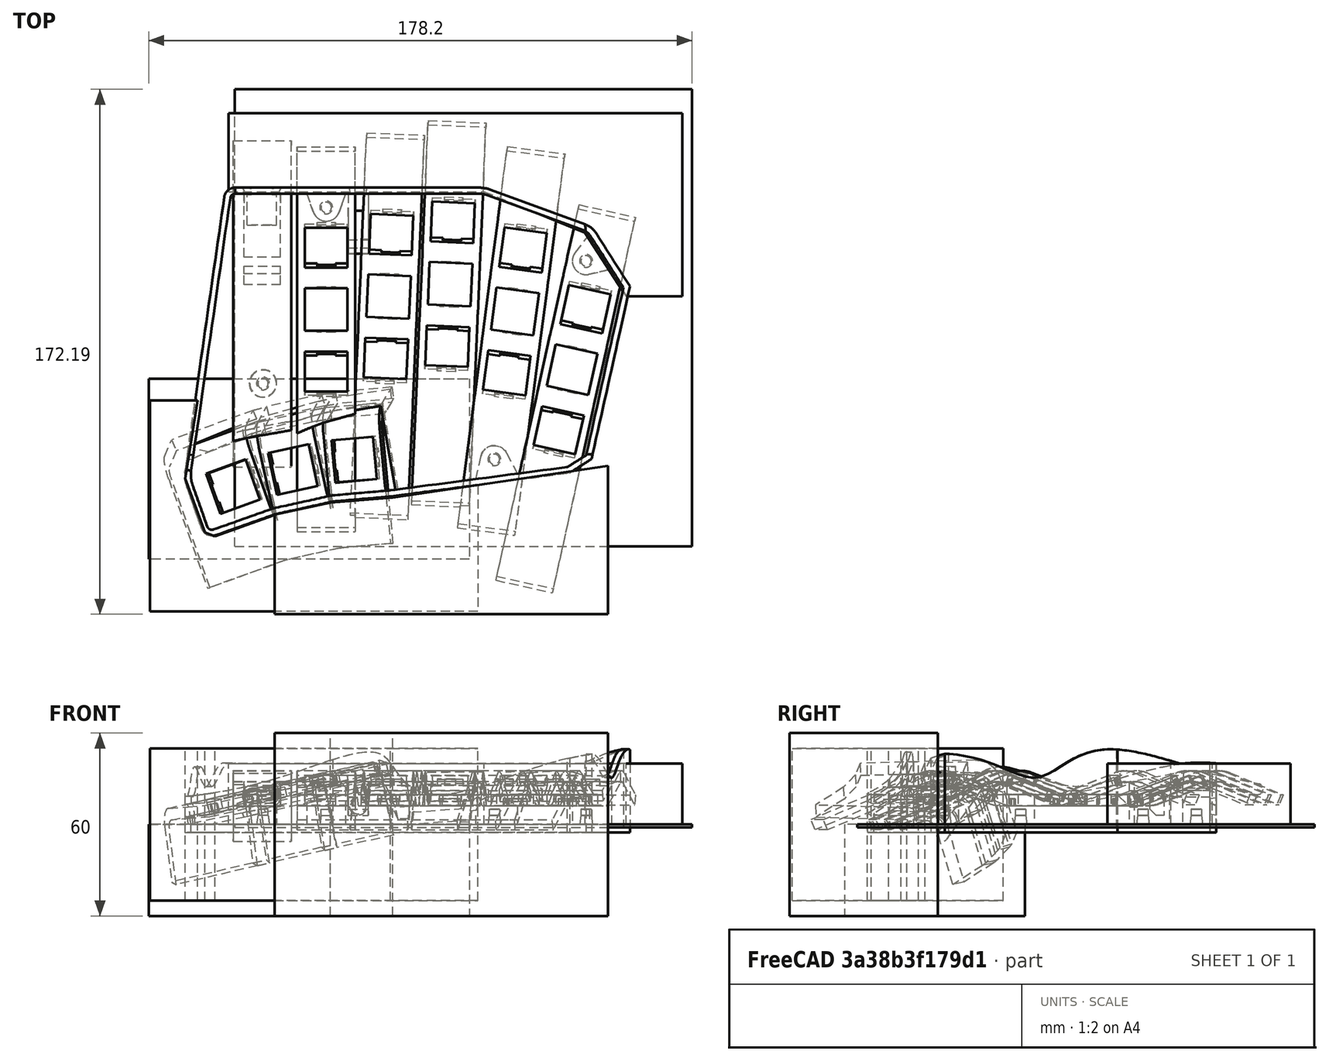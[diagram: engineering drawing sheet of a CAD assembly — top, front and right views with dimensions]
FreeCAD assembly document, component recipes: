
FREECAD ASSEMBLY — COMPONENT RECIPES ("KeyColumnArray2")

This assembly document has 28 components, labeled P0..P27 below (a component is one placed body or linked part). 20 of them carry a construction recipe — the FreeCAD feature program that regenerates the part from scratch, quoted from this document or its linked companion documents; the rest are supplied as boundary geometry only. No exploded tour is included for this assembly.
COMPONENT P0 — recipe-attached ("ShellRough", modeled in this document).
Construction recipe (the document's own serialized feature program — sketch geometry with constraints, then the solid features built on it; lengths are millimeters unless a unit is written):

FEATURE [Sketcher::SketchObject] Sketch
  FullyConstrained = false
  MapMode = 5
  Support = -> [XY_Plane001]
  sketch-geometry (20):
    g0: LineSegment StartX=-33.4431 StartY=36.9112 StartZ=0 EndX=-46.2795 EndY=-52.5754 EndZ=0
    g1: LineSegment StartX=-45.7128 StartY=-58.285 StartZ=0 EndX=-40.9023 EndY=-71.8694 EndZ=0
    g2: LineSegment StartX=-36.307 StartY=-74.0612 StartZ=0 EndX=-16.9221 EndY=-67.1967 EndZ=0
    g3: LineSegment StartX=-16.9221 StartY=-67.1967 StartZ=0 EndX=2.15083 EndY=-62.9753 EndZ=0
    g4: LineSegment StartX=2.15083 StartY=-62.9753 StartZ=0 EndX=21.2304 EndY=-61.306 EndZ=0
    g5: LineSegment StartX=21.2304 StartY=-61.306 StartZ=0 EndX=79.8355 EndY=-53.6064 EndZ=0
    g6: LineSegment StartX=79.8355 StartY=-53.6064 StartZ=0 EndX=87.0661 EndY=-49 EndZ=0
    g7: LineSegment StartX=87.0661 StartY=-49 StartZ=0 EndX=99.6141 EndY=7.6 EndZ=0
    g8: LineSegment StartX=99.6141 StartY=7.6 StartZ=0 EndX=88.4546 EndY=25.1169 EndZ=0
    g9: LineSegment StartX=84.9582 StartY=27.9288 StartZ=0 EndX=53.9986 EndY=39.268 EndZ=0
    g10: LineSegment StartX=49.8716 StartY=40 StartZ=0 EndX=-29.8796 EndY=40 EndZ=0
    g11: ArcOfCircle CenterX=-37.5088 CenterY=-70.6677 CenterZ=0 NormalX=0 NormalY=0 NormalZ=1 AngleXU=0 Radius=3.6 StartAngle=3.48193 EndAngle=5.05273
    g12: ArcOfCircle CenterX=-29.8796 CenterY=36.4 CenterZ=0 NormalX=0 NormalY=0 NormalZ=1 AngleXU=0 Radius=3.6 StartAngle=1.5708 EndAngle=2.99912
    g13: GeomPoint X=-33 Y=40 Z=0
    g14: ArcOfCircle CenterX=-34.4011 CenterY=-54.2793 CenterZ=0 NormalX=0 NormalY=0 NormalZ=1 AngleXU=0 Radius=12 StartAngle=2.99912 EndAngle=3.48193
    g15: GeomPoint X=-46.699 Y=-55.5 Z=0
    g16: ArcOfCircle CenterX=49.8716 CenterY=28 CenterZ=0 NormalX=0 NormalY=0 NormalZ=1 AngleXU=0 Radius=12 StartAngle=1.21971 EndAngle=1.5708
    g17: GeomPoint X=52 Y=40 Z=0
    g18: ArcOfCircle CenterX=82.5508 CenterY=21.3558 CenterZ=0 NormalX=0 NormalY=0 NormalZ=1 AngleXU=0 Radius=7 StartAngle=0.567232 EndAngle=1.21971
    g19: GeomPoint X=87.1821 Y=27.1143 Z=0
  constraints (43):
    c: Coincident(g2,g3)
    c: Coincident(g3,g4)
    c: Coincident(g4,g5)
    c: Coincident(g5,g6)
    c: Coincident(g6,g7)
    c: Coincident(g7,g8)
    c: Horizontal(g10)
    c: DistanceY(g-1,g17) = 40
    c: DistanceX(g-1,g17) = 52
    c: DistanceX(g13,g-1) = 33
    c: Angle(g-1,g7) = 1.35263
    c: Angle(g7,g6) = 2.35619
    c: Perpendicular(g2,g1)
    c: Angle(g-2,g1) = 0.340339
    c: DistanceY(g15,g-1) = 55.5
    c: Tangent(g1,g11) = -1.5708
    c: Tangent(g2,g11) = -1.5708
    c: Radius(g11) = 3.6
    c: Angle(g-2,g3) = 1.78861
    c: Angle(g4,g-2) = 1.48353
    c: PointOnObject(g13,g0)
    c: PointOnObject(g13,g10)
    c: Tangent(g0,g12) = -1.5708
    c: Tangent(g10,g12) = -1.5708
    c: Radius(g12) = 3.6
    c: PointOnObject(g15,g1)
    c: PointOnObject(g15,g0)
    c: Tangent(g1,g14) = -1.5708
    c: Tangent(g0,g14) = -1.5708
    c: Radius(g14) = 12
    c: PointOnObject(g17,g10)
    c: PointOnObject(g17,g9)
    c: Tangent(g10,g16) = -1.5708
    c: Tangent(g9,g16) = -1.5708
    c: Radius(g16) = 12
    c: PointOnObject(g19,g9)
    c: PointOnObject(g19,g8)
    c: Tangent(g9,g18) = -1.5708
    c: Tangent(g8,g18) = -1.5708
    c: Radius(g18) = 7
    c: Angle(g8,g7) = 2.35619
    c: DistanceY(g-1,g7) = 7.6
    c: DistanceY(g6,g-1) = 49
FEATURE [PartDesign::Pad] Pad
  Direction = (0,0,1)
  Length = 30
  Length2 = 10
  Profile = -> Sketch
  ReferenceAxis = -> Sketch [N_Axis]
  Type = 0
FEATURE [PartDesign::Thickness] Thickness
  Base = -> Pad [Face18,Face17]
  BaseFeature = -> Pad
  Intersection = false
  Join = 0
  Mode = 0
  Reversed = true
  SupportTransform = false
  Value = 2
FEATURE [PartDesign::Body] Body001  label="ShellRough"
  Group = -> [Sketch,Pad,Thickness]
  Origin = -> Origin001
  Tip = -> Thickness
COMPONENT P1 — recipe-attached ("ThumbCutterBotLeft", modeled in this document).
Construction recipe (the document's own serialized feature program — sketch geometry with constraints, then the solid features built on it; lengths are millimeters unless a unit is written):

FEATURE [Sketcher::SketchObject] Sketch002
  FullyConstrained = false
  MapMode = 5
  Support = -> [XY_Plane003]
  sketch-geometry (11):
    g0: LineSegment StartX=-57.8461 StartY=-29.8467 StartZ=0 EndX=-42.1659 EndY=-29.8467 EndZ=0
    g1: LineSegment StartX=-42.1659 StartY=-29.8467 StartZ=0 EndX=-46.2211 EndY=-55.5298 EndZ=0
    g2: LineSegment StartX=-46.2211 StartY=-55.5298 StartZ=0 EndX=-39.7328 EndY=-73.1024 EndZ=0
    g3: LineSegment StartX=-39.7328 StartY=-73.1024 StartZ=0 EndX=-36.4886 EndY=-74.4541 EndZ=0
    g4: LineSegment StartX=-36.4886 StartY=-74.4541 StartZ=0 EndX=-17.0235 EndY=-67.4251 EndZ=0
    g5: LineSegment StartX=-17.0235 StartY=-67.4251 StartZ=0 EndX=1.36017 EndY=-63.3699 EndZ=0
    g6: LineSegment StartX=1.36017 StartY=-63.3699 StartZ=0 EndX=21.0956 EndY=-61.4774 EndZ=0
    g7: LineSegment StartX=21.0956 StartY=-61.4774 StartZ=0 EndX=49.7525 EndY=-57.6925 EndZ=0
    g8: LineSegment StartX=49.7525 StartY=-57.6925 StartZ=0 EndX=49.7525 EndY=-99.0559 EndZ=0
    g9: LineSegment StartX=49.7525 StartY=-99.0559 StartZ=0 EndX=-57.8461 EndY=-99.0559 EndZ=0
    g10: LineSegment StartX=-57.8461 StartY=-99.0559 StartZ=0 EndX=-57.8461 EndY=-29.8467 EndZ=0
  constraints (15):
    c: Horizontal(g0)
    c: Coincident(g0,g1)
    c: Coincident(g1,g2)
    c: Coincident(g2,g3)
    c: Coincident(g3,g4)
    c: Coincident(g4,g5)
    c: Coincident(g5,g6)
    c: Coincident(g6,g7)
    c: Coincident(g7,g8)
    c: Vertical(g8)
    c: Coincident(g8,g9)
    c: Horizontal(g9)
    c: Coincident(g9,g10)
    c: Coincident(g10,g0)
    c: Vertical(g10)
FEATURE [PartDesign::Pad] Pad002
  Direction = (0,0,1)
  Length = 50
  Length2 = 10
  Midplane = true
  Profile = -> Sketch002
  ReferenceAxis = -> Sketch002 [N_Axis]
  Type = 0
FEATURE [PartDesign::Body] Body003  label="ThumbCutterBotLeft"
  Group = -> [Sketch002,Pad002]
  Origin = -> Origin003
  Tip = -> Pad002
COMPONENT P2 — recipe-attached ("ThumbCutterBottom", modeled in this document).
Construction recipe (the document's own serialized feature program — sketch geometry with constraints, then the solid features built on it; lengths are millimeters unless a unit is written):

FEATURE [Sketcher::SketchObject] Sketch003
  FullyConstrained = false
  MapMode = 5
  Support = -> [XY_Plane004]
  sketch-geometry (4):
    g0: LineSegment StartX=-58.202 StartY=-22.7672 StartZ=0 EndX=46.9496 EndY=-22.7672 EndZ=0
    g1: LineSegment StartX=46.9496 StartY=-22.7672 StartZ=0 EndX=46.9496 EndY=-81.8868 EndZ=0
    g2: LineSegment StartX=46.9496 StartY=-81.8868 StartZ=0 EndX=-58.202 EndY=-81.8868 EndZ=0
    g3: LineSegment StartX=-58.202 StartY=-81.8868 StartZ=0 EndX=-58.202 EndY=-22.7672 EndZ=0
  constraints (8):
    c: Coincident(g0,g1)
    c: Coincident(g1,g2)
    c: Coincident(g2,g3)
    c: Coincident(g3,g0)
    c: Horizontal(g0)
    c: Horizontal(g2)
    c: Vertical(g1)
    c: Vertical(g3)
FEATURE [PartDesign::Pad] Pad003
  Direction = (0,0,1)
  Length = 30
  Length2 = 10
  Profile = -> Sketch003
  ReferenceAxis = -> Sketch003 [N_Axis]
  Reversed = true
  Type = 0
FEATURE [PartDesign::Body] Body004  label="ThumbCutterBottom"
  Group = -> [Sketch003,Pad003]
  Origin = -> Origin004
  Tip = -> Pad003
COMPONENT P3 — recipe-attached ("UnderThumbCutter", modeled in this document).
Construction recipe (the document's own serialized feature program — sketch geometry with constraints, then the solid features built on it; lengths are millimeters unless a unit is written):

FEATURE [PartDesign::SubShapeBinder] Binder003  label="Big"
  BindCopyOnChange = 0
  BindMode = 0
  ClaimChildren = false
  Context = -> Body006 [Binder003.]
  Fuse = false
  MakeFace = true
  OffsetFill = false
  OffsetIntersection = false
  OffsetJoinType = 0
  OffsetOpenResult = false
  PartialLoad = false
  Relative = true
  Support = -> [Cut002[Edge44,Edge45,Edge46,Edge47]]
  _Version = 2
FEATURE [PartDesign::SubShapeBinder] Binder004  label="Small"
  BindCopyOnChange = 0
  BindMode = 0
  ClaimChildren = false
  Context = -> Body006 [Binder004.]
  Fuse = false
  MakeFace = true
  OffsetFill = false
  OffsetIntersection = false
  OffsetJoinType = 0
  OffsetOpenResult = false
  PartialLoad = false
  Relative = true
  Support = -> [Cut002[Edge127,Edge129,Edge130,Edge131]]
  _Version = 2
FEATURE [PartDesign::SubShapeBinder] Binder005  label="Path"
  BindCopyOnChange = 0
  BindMode = 0
  ClaimChildren = false
  Context = -> Body006 [Binder005.]
  Fuse = false
  MakeFace = true
  OffsetFill = false
  OffsetIntersection = false
  OffsetJoinType = 0
  OffsetOpenResult = false
  PartialLoad = false
  Relative = true
  Support = -> [Cut002[Edge127,Edge126,Edge123,Edge122,Edge109]]
  _Version = 2
FEATURE [Sketcher::SketchObject] Sketch005
  FullyConstrained = false
  Placement = pos=(-2.47193,-0.548013,11.4209) rot=(0.216439,-0.976296,0;0.218166rad)
  sketch-geometry (5):
    g0: LineSegment StartX=21.4334 StartY=-34.223 StartZ=0 EndX=2.51313 EndY=-35.9615 EndZ=0
    g1: BSplineCurve PolesCount=2 KnotsCount=2 Degree=1 IsPeriodic=0
    g2: LineSegment StartX=-1.05539 StartY=-36.5965 StartZ=0 EndX=-19.605 EndY=-40.7088 EndZ=0
    g3: BSplineCurve PolesCount=2 KnotsCount=2 Degree=1 IsPeriodic=0
    g4: LineSegment StartX=-23.1076 StartY=-41.6414 StartZ=0 EndX=-40.9899 EndY=-48.0619 EndZ=0
  constraints (4):
    c: Coincident(g0,g1)
    c: Coincident(g1,g2)
    c: Coincident(g2,g3)
    c: Coincident(g3,g4)
FEATURE [Sketcher::SketchObject] Sketch006
  FullyConstrained = false
  Placement = pos=(-50.3364,-18.2454,-11.7703) rot=(0.340774,-0.940145,0;1.78719rad)
  sketch-geometry (4):
    g0: LineSegment StartX=34.9538 StartY=-48.5618 StartZ=0 EndX=33.5799 EndY=-45.0789 EndZ=0
    g1: LineSegment StartX=33.5799 StartY=-45.0789 StartZ=0 EndX=26.6082 EndY=-27.4042 EndZ=0
    g2: ArcOfCircle CenterX=22.8872 CenterY=-28.8719 CenterZ=0 NormalX=0 NormalY=1e-16 NormalZ=1 AngleXU=-2.76588 Radius=4 StartAngle=1.5708 EndAngle=2.88852
    g3: LineSegment StartX=21.8685 StartY=-24.9672 StartZ=0 EndX=22.3979 EndY=-24.902 EndZ=0
  constraints (3):
    c: Coincident(g0,g1)
    c: Coincident(g1,g2)
    c: Coincident(g2,g3)
FEATURE [Sketcher::SketchObject] Sketch007
  FullyConstrained = false
  Placement = pos=(17.7176,1.57374,3.9103) rot=(-0.088475,0.996078,0;1.3544rad)
  sketch-geometry (6):
    g0: LineSegment StartX=-9.09004 StartY=-79.2968 StartZ=0 EndX=-11.138 EndY=-61.1386 EndZ=0
    g1: LineSegment StartX=-11.138 StartY=-61.1386 StartZ=0 EndX=-13.3253 EndY=-42.1061 EndZ=0
    g2: ArcOfCircle CenterX=-5.98227 CenterY=-40.8863 CenterZ=0 NormalX=1e-16 NormalY=0 NormalZ=1 AngleXU=-1.45423 Radius=7.44361 StartAngle=3.36428 EndAngle=4.76043
    g3: LineSegment StartX=9.38655 StartY=-26.7286 StartZ=0 EndX=-8.45934 EndY=-33.867 EndZ=0
    g4: LineSegment StartX=-9.09004 StartY=-79.2968 StartZ=0 EndX=18.9825 EndY=-76.3619 EndZ=0
    g5: LineSegment StartX=18.9825 StartY=-76.3619 StartZ=0 EndX=9.38655 EndY=-26.7286 EndZ=0
  constraints (6):
    c: Coincident(g0,g1)
    c: Coincident(g1,g2)
    c: Coincident(g2,g3)
    c: Coincident(g0,g4)
    c: Coincident(g4,g5)
    c: Coincident(g5,g3)
FEATURE [PartDesign::AdditivePipe] AdditivePipe
  AuxilleryCurvelinear = true
  AuxillerySpineTangent = false
  Binormal = (0,0,0)
  Mode = 0
  Placement = pos=(17.7176,1.57374,3.9103) rot=(-0.088475,0.996078,0;1.3544rad)
  Profile = -> Sketch007
  Spine = -> Binder005
  SpineTangent = false
  Transformation = 0
  Transition = 0
FEATURE [PartDesign::Body] Body006  label="UnderThumbCutter"
  Group = -> [Binder003,Binder004,Binder005,Sketch005,Sketch006,Sketch007,AdditivePipe]
  Origin = -> Origin006
  Tip = -> AdditivePipe
COMPONENT P4 — recipe-attached ("MCU-Holder", modeled in this document).
Construction recipe (the document's own serialized feature program — sketch geometry with constraints, then the solid features built on it; lengths are millimeters unless a unit is written):

FEATURE [Sketcher::SketchObject] Sketch008
  FullyConstrained = true
  MapMode = 5
  Placement = pos=(0,0,0) rot=(0.57735,0.57735,0.57735;2.0944rad)
  Support = -> [YZ_Plane007]
  sketch-geometry (8):
    g0: LineSegment StartX=-24 StartY=5.5 StartZ=0 EndX=-24 EndY=0 EndZ=0
    g1: LineSegment StartX=-24 StartY=0 StartZ=0 EndX=1.25 EndY=0 EndZ=0
    g2: LineSegment StartX=1.25 StartY=0 StartZ=0 EndX=1.25 EndY=-3.6 EndZ=0
    g3: LineSegment StartX=1.25 StartY=-3.6 StartZ=0 EndX=-4.9788 EndY=-4.78813 EndZ=0
    g4: LineSegment StartX=-4.9788 StartY=-4.78813 StartZ=0 EndX=-30.1 EndY=0 EndZ=0
    g5: LineSegment StartX=-30.1 StartY=0 StartZ=0 EndX=-30.1 EndY=2 EndZ=0
    g6: LineSegment StartX=-30.1 StartY=2 StartZ=0 EndX=-26.6 EndY=5.5 EndZ=0
    g7: LineSegment StartX=-26.6 StartY=5.5 StartZ=0 EndX=-24 EndY=5.5 EndZ=0
  constraints (24):
    c: PointOnObject(g0,g-1)
    c: Vertical(g0)
    c: Coincident(g0,g1)
    c: Horizontal(g1)
    c: Coincident(g1,g2)
    c: Vertical(g2)
    c: Coincident(g2,g3)
    c: Coincident(g3,g4)
    c: PointOnObject(g4,g-1)
    c: Coincident(g4,g5)
    c: Vertical(g5)
    c: Coincident(g5,g6)
    c: Coincident(g6,g7)
    c: Coincident(g7,g0)
    c: Horizontal(g7)
    c: DistanceX(g7,g7) = 2.6
    c: DistanceY(g0,g0) = 5.5
    c: DistanceX(g5,g6) = 3.5
    c: Angle(g6,g7) = 2.35619
    c: DistanceX(g0,g-1) = 24
    c: DistanceX(g-1,g1) = 1.25
    c: DistanceY(g2,g2) = 3.6
    c: DistanceX(g3) = -4.9788
    c: DistanceY(g3) = -4.78813
FEATURE [PartDesign::Pad] Pad005
  Direction = (1,-2e-16,3e-16)
  Length = 12
  Length2 = 10
  Midplane = true
  Placement = pos=(0,0,0) rot=(0.57735,0.57735,0.57735;2.0944rad)
  Profile = -> Sketch008
  ReferenceAxis = -> Sketch008 [N_Axis]
  Type = 0
FEATURE [PartDesign::Body] Body007  label="MCU-Holder"
  Group = -> [Sketch008,Pad005]
  Origin = -> Origin007
  Placement = pos=(-21,38.25,11.25) rot=(0,1,0;3.14159rad)
  Tip = -> Pad005
COMPONENT P5 — geometry summary ("ShellCutterPart"; no construction recipe available for this part):
  bounding box: 146.0 x 114.3 x 30.0 mm
  tessellated surface: 412 triangles
  volume: 395667 mm^3 (79% of its bounding box)
  symmetry: mirror-symmetric across its z mid-plane
COMPONENT P6 — recipe-attached ("ThumbTriangleCutter", modeled in this document).
Construction recipe (the document's own serialized feature program — sketch geometry with constraints, then the solid features built on it; lengths are millimeters unless a unit is written):

FEATURE [PartDesign::SubShapeBinder] Binder008
  BindCopyOnChange = 0
  BindMode = 0
  ClaimChildren = false
  Context = -> Body010 [Binder008.]
  Fuse = false
  MakeFace = true
  OffsetFill = false
  OffsetIntersection = false
  OffsetJoinType = 0
  OffsetOpenResult = false
  PartialLoad = false
  Relative = true
  Support = -> [Common[Face16,Face15,Face14,Face13,Face12]]
  _Version = 2
FEATURE [PartDesign::SubShapeBinder] Binder009
  BindCopyOnChange = 0
  BindMode = 0
  ClaimChildren = false
  Context = -> Body010 [Binder009.]
  Fuse = false
  MakeFace = true
  OffsetFill = false
  OffsetIntersection = false
  OffsetJoinType = 0
  OffsetOpenResult = false
  PartialLoad = false
  Relative = true
  Support = -> [Common[Face6,Face7,Face8,Face9,Face10]]
  _Version = 2
FEATURE [PartDesign::Plane] DatumPlane
  Length = 90.3213
  MapMode = 45
  Placement = pos=(10.8462,-31.5971,6.48979) rot=(-0.487707,-0.562269,-0.667829;1.80626rad)
  ResizeMode = 0
  Support = -> [Binder008,Binder009]
  Width = 97.1376
FEATURE [Sketcher::SketchObject] Sketch010
  FullyConstrained = false
  MapMode = 5
  Placement = pos=(10.8462,-31.5971,6.48979) rot=(-0.487707,-0.562269,-0.667829;1.80626rad)
  Support = -> [DatumPlane]
  sketch-geometry (7):
    g0: LineSegment StartX=-5.99127 StartY=-62.4069 StartZ=0 EndX=-2.7146 EndY=-38.9241 EndZ=0
    g1: LineSegment StartX=-2.7146 StartY=-38.9241 StartZ=0 EndX=-1.48585 EndY=-31.6881 EndZ=0
    g2: LineSegment StartX=-1.48585 StartY=-31.6881 StartZ=0 EndX=1.51776 EndY=-16.1239 EndZ=0
    g3: LineSegment StartX=1.51776 StartY=-16.1239 StartZ=0 EndX=2.88304 EndY=-9.5706 EndZ=0
    g4: LineSegment StartX=2.88304 StartY=-9.5706 StartZ=0 EndX=7.38846 EndY=8.9972 EndZ=0
    g5: LineSegment StartX=7.38846 StartY=8.9972 StartZ=0 EndX=-10.3602 EndY=14.0487 EndZ=0
    g6: LineSegment StartX=-10.3602 StartY=14.0487 StartZ=0 EndX=-5.99127 EndY=-62.4069 EndZ=0
  constraints (7):
    c: Coincident(g0,g1)
    c: Coincident(g1,g2)
    c: Coincident(g2,g3)
    c: Coincident(g3,g4)
    c: Coincident(g4,g5)
    c: Coincident(g5,g6)
    c: Coincident(g6,g0)
FEATURE [PartDesign::Pad] Pad007
  Direction = (-0.145065,0.93735,0.31675)
  Length = 20
  Length2 = 10
  Midplane = true
  Placement = pos=(10.8462,-31.5971,6.48979) rot=(-0.487707,-0.562269,-0.667829;1.80626rad)
  Profile = -> Sketch010
  ReferenceAxis = -> Sketch010 [N_Axis]
  Type = 0
FEATURE [PartDesign::Body] Body010  label="ThumbTriangleCutter"
  Group = -> [Binder008,Binder009,DatumPlane,Sketch010,Pad007]
  Origin = -> Origin010
  Tip = -> Pad007
COMPONENT P7 — recipe-attached ("WaveFront", modeled in this document).
Construction recipe (the document's own serialized feature program — sketch geometry with constraints, then the solid features built on it; lengths are millimeters unless a unit is written):

FEATURE [Sketcher::SketchObject] Sketch011
  FullyConstrained = false
  MapMode = 5
  Placement = pos=(0,0,0) rot=(1,0,0;1.5708rad)
  Support = -> [XZ_Plane011]
  sketch-geometry (23):
    g0: LineSegment StartX=-51.25 StartY=39.47 StartZ=0 EndX=-51.25 EndY=8.74275 EndZ=0
    g1: LineSegment StartX=-51.25 StartY=8.74275 StartZ=0 EndX=18.1024 EndY=24.754 EndZ=0
    g2: LineSegment StartX=22.4199 StartY=22.0561 StartZ=0 EndX=24.2026 EndY=14.3346 EndZ=0
    g3: LineSegment StartX=28.2541 StartY=11.5857 StartZ=0 EndX=107.47 EndY=23.6899 EndZ=0
    g4: LineSegment StartX=107.47 StartY=23.6899 StartZ=0 EndX=107.47 EndY=39.47 EndZ=0
    g5: LineSegment StartX=107.47 StartY=39.47 StartZ=0 EndX=-51.25 EndY=39.47 EndZ=0
    g6: ArcOfCircle CenterX=18.9122 CenterY=21.2463 CenterZ=0 NormalX=0 NormalY=0 NormalZ=1 AngleXU=0 Radius=3.6 StartAngle=0.226893 EndAngle=1.79769
    g7: ArcOfCircle CenterX=27.7103 CenterY=15.1444 CenterZ=0 NormalX=0 NormalY=0 NormalZ=1 AngleXU=0 Radius=3.6 StartAngle=3.36849 EndAngle=4.86402
    g8-g15: Circle x8 (B-spline internal-alignment scaffolding for g16; pole/knot coordinates omitted)
    g16: BSplineCurve PolesCount=8 KnotsCount=6 Degree=3 IsPeriodic=0
    g17-g22: GeomPoint x6 (B-spline internal-alignment scaffolding for g16; pole/knot coordinates omitted)
  constraints (24):
    c: Vertical(g0)
    c: Coincident(g0,g1)
    c: Coincident(g3,g4)
    c: Vertical(g4)
    c: Coincident(g4,g5)
    c: Coincident(g5,g0)
    c: Horizontal(g5)
    c: Tangent(g1,g6) = 1.5708
    c: Tangent(g2,g6) = 1.5708
    c: Tangent(g2,g7) = -1.5708
    c: Tangent(g3,g7) = -1.5708
    c: Radius(g6) = 3.6
    c: Radius(g7) = 3.6
    c: DistanceX(g0,g-1) = 51.25
    c: DistanceX(g-1,g3) = 107.47
    c: DistanceY(g-1,g0) = 39.47
    c: Angle(g-1,g1) = 0.226893
    c: Perpendicular(g2,g1)
    c: Weight(g8) = 1
    c: Coincident(g16,g0)
    c: Equal(g8, g9-g15) x7
    c: Coincident(g16,g4)
    c: InternalAlignment(g8-g15 -> g16) x8
    c: InternalAlignment(g17-g22 -> g16) x6
FEATURE [PartDesign::Pad] Pad008
  Direction = (0,-1,2e-16)
  Length = 40
  Length2 = 10
  Placement = pos=(0,0,0) rot=(1,0,0;1.5708rad)
  Profile = -> Sketch011
  ReferenceAxis = -> Sketch011 [N_Axis]
  Type = 0
FEATURE [PartDesign::Body] Body011  label="WaveFront"
  Group = -> [Sketch011,Pad008]
  Origin = -> Origin011
  Placement = pos=(0,-47.5,0) rot=(0,0,1;0rad)
  Tip = -> Pad008
COMPONENT P8 — recipe-attached ("WaveLeft", modeled in this document).
Construction recipe (the document's own serialized feature program — sketch geometry with constraints, then the solid features built on it; lengths are millimeters unless a unit is written):

FEATURE [PartDesign::SubShapeBinder] Binder010
  BindCopyOnChange = 0
  BindMode = 0
  ClaimChildren = false
  Context = -> Body012 [Binder010.]
  Fuse = false
  MakeFace = true
  OffsetFill = false
  OffsetIntersection = false
  OffsetJoinType = 0
  OffsetOpenResult = false
  PartialLoad = false
  Relative = true
  Support = -> [Cut004[Face1]]
  _Version = 2
FEATURE [Sketcher::SketchObject] Sketch012
  ExternalGeometry = -> [Binder010]
  FullyConstrained = false
  MapMode = 5
  Placement = pos=(0,0,0) rot=(0.57735,0.57735,0.57735;2.0944rad)
  Support = -> [YZ_Plane012]
  sketch-geometry (23):
    g0: LineSegment StartX=-52.5227 StartY=18.3739 StartZ=0 EndX=-52.5227 EndY=37.6741 EndZ=0
    g1: LineSegment StartX=-52.5227 StartY=37.6741 StartZ=0 EndX=56.4163 EndY=37.6741 EndZ=0
    g2: LineSegment StartX=56.4163 StartY=9.13411 StartZ=0 EndX=51.2893 EndY=9.20452 EndZ=0
    g3-g12: Circle x10 (B-spline internal-alignment scaffolding for g13; pole/knot coordinates omitted)
    g13: BSplineCurve PolesCount=10 KnotsCount=8 Degree=3 IsPeriodic=0
    g14-g21: GeomPoint x8 (B-spline internal-alignment scaffolding for g13; pole/knot coordinates omitted)
    g22: LineSegment StartX=56.4163 StartY=9.13411 StartZ=0 EndX=56.4163 EndY=37.6741 EndZ=0
  constraints (16):
    c: Vertical(g0)
    c: Coincident(g0,g1)
    c: Horizontal(g1)
    c: DistanceX(g0) = -52.5227
    c: DistanceY(g0) = 18.3739
    c: Coincident(g-3,g2)
    c: Weight(g3) = 1
    c: Coincident(g13,g0)
    c: Equal(g3, g4-g12) x9
    c: Coincident(g13,g2)
    c: InternalAlignment(g3-g12 -> g13) x10
    c: InternalAlignment(g14-g21 -> g13) x8
    c: Coincident(g22,g2)
    c: Vertical(g22)
    c: Coincident(g22,g1)
    c: DistanceY(g22,g22) = 28.54
FEATURE [PartDesign::Pad] Pad009
  Direction = (1,-2e-16,3e-16)
  Length = 10
  Length2 = 10
  Placement = pos=(0,0,0) rot=(1,1,1;2.0944rad)
  Profile = -> Sketch012
  ReferenceAxis = -> Sketch012 [N_Axis]
  Type = 0
FEATURE [PartDesign::Body] Body012  label="WaveLeft"
  Group = -> [Sketch012,Pad009,Binder010]
  Origin = -> Origin012
  Placement = pos=(-33.6897,2.67023,0) rot=(0,0,1;3.01069rad)
  Tip = -> Pad009
COMPONENT P9 — recipe-attached ("WaveRight", modeled in this document).
Construction recipe (the document's own serialized feature program — sketch geometry with constraints, then the solid features built on it; lengths are millimeters unless a unit is written):

FEATURE [PartDesign::SubShapeBinder] Binder011
  BindCopyOnChange = 0
  BindMode = 0
  ClaimChildren = false
  Context = -> Body013 [Binder011.]
  Fuse = false
  MakeFace = true
  OffsetFill = false
  OffsetIntersection = false
  OffsetJoinType = 0
  OffsetOpenResult = false
  PartialLoad = false
  Relative = true
  Support = -> [Cut005[Face14],Cut006[Face14,Face17]]
  _Version = 2
FEATURE [Sketcher::SketchObject] Sketch013
  ExternalGeometry = -> [Binder011]
  FullyConstrained = false
  MapMode = 5
  Placement = pos=(0,0,0) rot=(0.57735,0.57735,0.57735;2.0944rad)
  Support = -> [YZ_Plane013]
  sketch-geometry (21):
    g0: LineSegment StartX=27.9295 StartY=20.0186 StartZ=0 EndX=32.9295 EndY=20.0186 EndZ=0
    g1: LineSegment StartX=32.9295 StartY=20.0186 StartZ=0 EndX=32.9295 EndY=40.0186 EndZ=0
    g2: LineSegment StartX=32.9295 StartY=40.0186 StartZ=0 EndX=-53.0705 EndY=40.0186 EndZ=0
    g3: LineSegment StartX=-53.0705 StartY=40.0186 StartZ=0 EndX=-53.0705 EndY=23.1665 EndZ=0
    g4: LineSegment StartX=-53.0705 StartY=23.1665 StartZ=0 EndX=-49 EndY=23.1665 EndZ=0
    g5: LineSegment StartX=-49 StartY=23.1665 StartZ=0 EndX=-47.5 EndY=23.2158 EndZ=0
    g6-g13: Circle x8 (B-spline internal-alignment scaffolding for g14; pole/knot coordinates omitted)
    g14: BSplineCurve PolesCount=8 KnotsCount=6 Degree=3 IsPeriodic=0
    g15-g20: GeomPoint x6 (B-spline internal-alignment scaffolding for g14; pole/knot coordinates omitted)
  constraints (22):
    c: Coincident(g0,g-5)
    c: Horizontal(g0)
    c: Coincident(g0,g1)
    c: Vertical(g1)
    c: Coincident(g1,g2)
    c: Horizontal(g2)
    c: Coincident(g2,g3)
    c: Vertical(g3)
    c: Coincident(g3,g4)
    c: Coincident(g4,g-3)
    c: Horizontal(g4)
    c: DistanceX(g0,g0) = 5
    c: DistanceY(g1,g1) = 20
    c: DistanceX(g2,g2) = 86
    c: Coincident(g5,g4)
    c: Coincident(g5,g-4)
    c: Weight(g6) = 1
    c: Coincident(g14,g5)
    c: Equal(g6, g7-g13) x7
    c: InternalAlignment(g6-g13 -> g14) x8
    c: InternalAlignment(g15-g20 -> g14) x6
    c: Coincident(g14,g0)
FEATURE [PartDesign::Pad] Pad010
  Direction = (1,-2e-16,3e-16)
  Length = 20
  Length2 = 10
  Placement = pos=(0,0,0) rot=(1,1,1;2.0944rad)
  Profile = -> Sketch013
  ReferenceAxis = -> Sketch013 [N_Axis]
  Type = 0
FEATURE [PartDesign::Body] Body013  label="WaveRight"
  Group = -> [Sketch013,Binder011,Pad010]
  Origin = -> Origin013
  Placement = pos=(84.75,0,0) rot=(0,0,1;0rad)
  Tip = -> Pad010
COMPONENT P10 — recipe-attached ("WaveBack", modeled in this document).
Construction recipe (the document's own serialized feature program — sketch geometry with constraints, then the solid features built on it; lengths are millimeters unless a unit is written):

FEATURE [PartDesign::SubShapeBinder] Binder012
  BindCopyOnChange = 0
  BindMode = 0
  ClaimChildren = false
  Context = -> Body014 [Binder012.]
  Fuse = false
  MakeFace = true
  OffsetFill = false
  OffsetIntersection = false
  OffsetJoinType = 0
  OffsetOpenResult = false
  PartialLoad = false
  Relative = true
  Support = -> [Cut005[Face19]]
  _Version = 2
FEATURE [Sketcher::SketchObject] Sketch014
  ExternalGeometry = -> [Binder012]
  FullyConstrained = true
  MapMode = 5
  Placement = pos=(0,0,0) rot=(1,0,0;1.5708rad)
  Support = -> [XZ_Plane014]
  sketch-geometry (5):
    g0: LineSegment StartX=28.1063 StartY=20.0186 StartZ=0 EndX=28.1063 EndY=32.3895 EndZ=0
    g1: LineSegment StartX=28.1063 StartY=32.3895 StartZ=0 EndX=-86.0937 EndY=32.3895 EndZ=0
    g2: LineSegment StartX=-86.0937 StartY=20.0186 StartZ=0 EndX=-86.0937 EndY=32.3895 EndZ=0
    g3: LineSegment StartX=27.003 StartY=20.0186 StartZ=0 EndX=28.1063 EndY=20.0186 EndZ=0
    g4: LineSegment StartX=27.003 StartY=20.0186 StartZ=0 EndX=-86.0937 EndY=20.0186 EndZ=0
  constraints (14):
    c: Vertical(g0)
    c: Horizontal(g1)
    c: Coincident(g2,g1)
    c: Vertical(g2)
    c: DistanceX(g0) = 28.1063
    c: DistanceY(g0) = 32.3895
    c: DistanceX(g1) = -86.0937
    c: Coincident(g3,g-3)
    c: Coincident(g3,g0)
    c: Horizontal(g3)
    c: Coincident(g4,g3)
    c: Coincident(g4,g2)
    c: Horizontal(g4)
    c: Coincident(g0,g1)
FEATURE [PartDesign::Pad] Pad011
  Direction = (0,-1,2e-16)
  Length = 25
  Length2 = 10
  Placement = pos=(0,0,0) rot=(1,0,0;1.5708rad)
  Profile = -> Sketch014
  ReferenceAxis = -> Sketch014 [N_Axis]
  Type = 0
FEATURE [PartDesign::Body] Body014  label="WaveBack"
  Group = -> [Sketch014,Binder012,Pad011]
  Origin = -> Origin014
  Placement = pos=(-0.959627,21.9791,0) rot=(0,0,1;3.18523rad)
  Tip = -> Pad011
COMPONENT P11 — recipe-attached ("HeatsetTopRightB", modeled in this document).
Construction recipe (the document's own serialized feature program — sketch geometry with constraints, then the solid features built on it; lengths are millimeters unless a unit is written):

FEATURE [PartDesign::SubShapeBinder] Binder013
  BindCopyOnChange = 0
  BindMode = 0
  ClaimChildren = false
  Context = -> Body015 [Binder013.]
  Fuse = false
  MakeFace = true
  OffsetFill = false
  OffsetIntersection = false
  OffsetJoinType = 0
  OffsetOpenResult = false
  PartialLoad = false
  Relative = true
  Support = -> [Link014[Face5]]
  _Version = 2
FEATURE [PartDesign::SubShapeBinder] Binder014
  BindCopyOnChange = 0
  BindMode = 0
  ClaimChildren = false
  Context = -> Body015 [Binder014.]
  Fuse = false
  MakeFace = true
  OffsetFill = false
  OffsetIntersection = false
  OffsetJoinType = 0
  OffsetOpenResult = false
  PartialLoad = false
  Relative = true
  Support = -> [Cut[Face121,Face122]]
  _Version = 2
FEATURE [PartDesign::Plane] DatumPlane001
  AttachmentOffset = pos=(0,0,-1) rot=(0,0,1;0rad)
  Length = 142.003
  MapMode = 5
  Placement = pos=(2.15678,9.72862,24.0572) rot=(0.999108,-0.008064,-0.041448;2.75764rad)
  ResizeMode = 0
  Support = -> [Binder014]
  Width = 83.1198
FEATURE [PartDesign::Pad] Pad012
  Direction = (-7.1e-15,1e-16,1)
  Length = 10
  Length2 = 10
  Profile = -> Binder013
  Type = 0
FEATURE [Sketcher::SketchObject] Sketch015
  FullyConstrained = false
  MapMode = 5
  Placement = pos=(2.15678,9.72862,24.0572) rot=(0.999108,-0.008064,-0.041448;2.75764rad)
  Support = -> [DatumPlane001]
  sketch-geometry (4):
    g0: LineSegment StartX=71.9341 StartY=3.84978 StartZ=0 EndX=100.189 EndY=3.84978 EndZ=0
    g1: LineSegment StartX=100.189 StartY=3.84978 StartZ=0 EndX=100.189 EndY=-25.5581 EndZ=0
    g2: LineSegment StartX=100.189 StartY=-25.5581 StartZ=0 EndX=71.9341 EndY=-25.5581 EndZ=0
    g3: LineSegment StartX=71.9341 StartY=-25.5581 StartZ=0 EndX=71.9341 EndY=3.84978 EndZ=0
  constraints (8):
    c: Coincident(g0,g1)
    c: Coincident(g1,g2)
    c: Coincident(g2,g3)
    c: Coincident(g3,g0)
    c: Horizontal(g0)
    c: Horizontal(g2)
    c: Vertical(g1)
    c: Vertical(g3)
FEATURE [PartDesign::Pocket] Pocket
  BaseFeature = -> Pad012
  Direction = (0.0828278,0.373612,0.92388)
  Length = 5
  Length2 = 5
  Profile = -> Sketch015
  ReferenceAxis = -> Sketch015 [N_Axis]
  Type = 1
FEATURE [PartDesign::Body] Body015  label="HeatsetTopRightB"
  Group = -> [Binder013,Binder014,DatumPlane001,Pad012,Sketch015,Pocket]
  Origin = -> Origin015
  Tip = -> Pocket
COMPONENT P12 — recipe-attached ("HeatsetBotRightB", modeled in this document).
Construction recipe (the document's own serialized feature program — sketch geometry with constraints, then the solid features built on it; lengths are millimeters unless a unit is written):

FEATURE [PartDesign::SubShapeBinder] Binder015
  BindCopyOnChange = 0
  BindMode = 0
  ClaimChildren = false
  Context = -> Body016 [Binder015.]
  Fuse = false
  MakeFace = true
  OffsetFill = false
  OffsetIntersection = false
  OffsetJoinType = 0
  OffsetOpenResult = false
  PartialLoad = false
  Relative = true
  Support = -> [Link017[Face5]]
  _Version = 2
FEATURE [PartDesign::SubShapeBinder] Binder016
  BindCopyOnChange = 0
  BindMode = 0
  ClaimChildren = false
  Context = -> Body016 [Binder016.]
  Fuse = false
  MakeFace = true
  OffsetFill = false
  OffsetIntersection = false
  OffsetJoinType = 0
  OffsetOpenResult = false
  PartialLoad = false
  Relative = true
  Support = -> [Cut[Face43]]
  _Version = 2
FEATURE [PartDesign::Plane] DatumPlane002
  AttachmentOffset = pos=(0,0,-1) rot=(0,0,1;0rad)
  Length = 109.912
  MapMode = 5
  Placement = pos=(-1.19259,-9.05864,22.0582) rot=(0.999676,-0.00493,0.024983;3.53114rad)
  ResizeMode = 0
  Support = -> [Binder016]
  Width = 110.591
FEATURE [PartDesign::Pad] Pad013
  Direction = (0,-7.1e-15,1)
  Length = 10
  Length2 = 10
  Profile = -> Binder015
  Type = 0
FEATURE [Sketcher::SketchObject] Sketch016
  FullyConstrained = false
  MapMode = 5
  Placement = pos=(-1.19259,-9.05864,22.0582) rot=(0.999676,-0.00493,0.024983;3.53114rad)
  Support = -> [DatumPlane002]
  sketch-geometry (4):
    g0: LineSegment StartX=46.0275 StartY=55.406 StartZ=0 EndX=70.6938 EndY=55.406 EndZ=0
    g1: LineSegment StartX=70.6938 StartY=55.406 StartZ=0 EndX=70.6938 EndY=33.1378 EndZ=0
    g2: LineSegment StartX=70.6938 StartY=33.1378 StartZ=0 EndX=46.0275 EndY=33.1378 EndZ=0
    g3: LineSegment StartX=46.0275 StartY=33.1378 StartZ=0 EndX=46.0275 EndY=55.406 EndZ=0
  constraints (8):
    c: Coincident(g0,g1)
    c: Coincident(g1,g2)
    c: Coincident(g2,g3)
    c: Coincident(g3,g0)
    c: Horizontal(g0)
    c: Horizontal(g2)
    c: Vertical(g1)
    c: Vertical(g3)
FEATURE [PartDesign::Pocket] Pocket001
  BaseFeature = -> Pad013
  Direction = (-0.0499502,-0.37941,0.92388)
  Length = 5
  Length2 = 5
  Profile = -> Sketch016
  ReferenceAxis = -> Sketch016 [N_Axis]
  Type = 1
FEATURE [PartDesign::Body] Body016  label="HeatsetBotRightB"
  Group = -> [Binder015,Binder016,DatumPlane002,Pad013,Sketch016,Pocket001]
  Origin = -> Origin016
  Tip = -> Pocket001
COMPONENT P13 — recipe-attached ("HeatsetTopLeftB", modeled in this document).
Construction recipe (the document's own serialized feature program — sketch geometry with constraints, then the solid features built on it; lengths are millimeters unless a unit is written):

FEATURE [PartDesign::SubShapeBinder] Binder017
  BindCopyOnChange = 0
  BindMode = 0
  ClaimChildren = false
  Context = -> Body017 [Binder017.]
  Fuse = false
  MakeFace = true
  OffsetFill = false
  OffsetIntersection = false
  OffsetJoinType = 0
  OffsetOpenResult = false
  PartialLoad = false
  Relative = true
  Support = -> [Link015[Face5]]
  _Version = 2
FEATURE [PartDesign::SubShapeBinder] Binder018
  BindCopyOnChange = 0
  BindMode = 0
  ClaimChildren = false
  Context = -> Body017 [Binder018.]
  Fuse = false
  MakeFace = true
  OffsetFill = false
  OffsetIntersection = false
  OffsetJoinType = 0
  OffsetOpenResult = false
  PartialLoad = false
  Relative = true
  Support = -> [Cut[Face256]]
  _Version = 2
FEATURE [PartDesign::Plane] DatumPlane003
  AttachmentOffset = pos=(0,0,-0.5) rot=(0,0,1;0rad)
  Length = 62.5507
  MapMode = 5
  Placement = pos=(0,10.3934,25.092) rot=(1,0,0;2.74889rad)
  ResizeMode = 0
  Support = -> [Binder018]
  Width = 91.3103
FEATURE [PartDesign::Pad] Pad014
  Direction = (0,3.6e-15,1)
  Length = 10
  Length2 = 10
  Profile = -> Binder017
  Type = 0
FEATURE [Sketcher::SketchObject] Sketch017
  FullyConstrained = false
  MapMode = 5
  Placement = pos=(0,10.3934,25.092) rot=(1,0,0;2.74889rad)
  Support = -> [DatumPlane003]
  sketch-geometry (4):
    g0: LineSegment StartX=-10.4446 StartY=-17.1438 StartZ=0 EndX=9.93344 EndY=-17.1438 EndZ=0
    g1: LineSegment StartX=9.93344 StartY=-17.1438 StartZ=0 EndX=9.93344 EndY=-38.4316 EndZ=0
    g2: LineSegment StartX=9.93344 StartY=-38.4316 StartZ=0 EndX=-10.4446 EndY=-38.4316 EndZ=0
    g3: LineSegment StartX=-10.4446 StartY=-38.4316 StartZ=0 EndX=-10.4446 EndY=-17.1438 EndZ=0
  constraints (8):
    c: Coincident(g0,g1)
    c: Coincident(g1,g2)
    c: Coincident(g2,g3)
    c: Coincident(g3,g0)
    c: Horizontal(g0)
    c: Horizontal(g2)
    c: Vertical(g1)
    c: Vertical(g3)
FEATURE [PartDesign::Pocket] Pocket002
  BaseFeature = -> Pad014
  Direction = (0,0.382683,0.92388)
  Length = 5
  Length2 = 5
  Profile = -> Sketch017
  ReferenceAxis = -> Sketch017 [N_Axis]
  Type = 1
FEATURE [PartDesign::Body] Body017  label="HeatsetTopLeftB"
  Group = -> [Binder017,Binder018,DatumPlane003,Pad014,Sketch017,Pocket002]
  Origin = -> Origin017
  Placement = pos=(0,0,-1) rot=(0,0,1;0rad)
  Tip = -> Pocket002
COMPONENT P14 — recipe-attached ("HeatsetBotLeftB", modeled in this document).
Construction recipe (the document's own serialized feature program — sketch geometry with constraints, then the solid features built on it; lengths are millimeters unless a unit is written):

FEATURE [PartDesign::SubShapeBinder] Binder019
  BindCopyOnChange = 0
  BindMode = 0
  ClaimChildren = false
  Context = -> Body018 [Binder019.]
  Fuse = false
  MakeFace = true
  OffsetFill = false
  OffsetIntersection = false
  OffsetJoinType = 0
  OffsetOpenResult = false
  PartialLoad = false
  Relative = true
  Support = -> [Link019[Face3]]
  _Version = 2
FEATURE [PartDesign::SubShapeBinder] Binder020
  BindCopyOnChange = 0
  BindMode = 0
  ClaimChildren = false
  Context = -> Body018 [Binder020.]
  Fuse = false
  MakeFace = true
  OffsetFill = false
  OffsetIntersection = false
  OffsetJoinType = 0
  OffsetOpenResult = false
  PartialLoad = false
  Relative = true
  Support = -> [Cut[Face10]]
  _Version = 2
FEATURE [PartDesign::Pad] Pad015
  Direction = (0,-3.6e-15,1)
  Length = 10
  Length2 = 10
  Profile = -> Binder019
  Type = 0
FEATURE [PartDesign::Plane] DatumPlane004
  Length = 67.9405
  MapMode = 5
  Placement = pos=(9.64605e-08,0.638829,1.66421) rot=(1,0,0;2.77507rad)
  ResizeMode = 0
  Support = -> [Binder020]
  Width = 82.1551
FEATURE [Sketcher::SketchObject] Sketch018
  FullyConstrained = false
  MapMode = 5
  Placement = pos=(9.64605e-08,0.638829,1.66421) rot=(1,0,0;2.77507rad)
  Support = -> [DatumPlane004]
  sketch-geometry (4):
    g0: LineSegment StartX=-31.4694 StartY=34.0482 StartZ=0 EndX=-9.71055 EndY=34.0482 EndZ=0
    g1: LineSegment StartX=-9.71055 StartY=34.0482 StartZ=0 EndX=-9.71055 EndY=12.4986 EndZ=0
    g2: LineSegment StartX=-9.71055 StartY=12.4986 StartZ=0 EndX=-31.4694 EndY=12.4986 EndZ=0
    g3: LineSegment StartX=-31.4694 StartY=12.4986 StartZ=0 EndX=-31.4694 EndY=34.0482 EndZ=0
  constraints (8):
    c: Coincident(g0,g1)
    c: Coincident(g1,g2)
    c: Coincident(g2,g3)
    c: Coincident(g3,g0)
    c: Horizontal(g0)
    c: Horizontal(g2)
    c: Vertical(g1)
    c: Vertical(g3)
FEATURE [PartDesign::Pocket] Pocket003
  BaseFeature = -> Pad015
  Direction = (5.41121e-08,0.358368,0.93358)
  Length = 5
  Length2 = 5
  Profile = -> Sketch018
  ReferenceAxis = -> Sketch018 [N_Axis]
  Type = 1
FEATURE [PartDesign::Body] Body018  label="HeatsetBotLeftB"
  Group = -> [Binder019,Binder020,Pad015,DatumPlane004,Sketch018,Pocket003]
  Origin = -> Origin018
  Tip = -> Pocket003
COMPONENT P15 — recipe-attached ("ShellSkirt", modeled in this document).
Construction recipe (the document's own serialized feature program — sketch geometry with constraints, then the solid features built on it; lengths are millimeters unless a unit is written):

FEATURE [PartDesign::SubShapeBinder] Binder021
  BindCopyOnChange = 0
  BindMode = 0
  ClaimChildren = false
  Context = -> Body020 [Binder021.]
  Fuse = false
  MakeFace = true
  OffsetFill = false
  OffsetIntersection = false
  OffsetJoinType = 0
  OffsetOpenResult = false
  PartialLoad = false
  Relative = true
  Support = -> [Cut007[Face2]]
  _Version = 2
FEATURE [PartDesign::Pad] Pad016
  Direction = (0,0,-1)
  Length = 2.6
  Length2 = 10
  Profile = -> Binder021
  Type = 0
FEATURE [PartDesign::Body] Body020  label="ShellSkirt"
  Group = -> [Binder021,Pad016]
  Origin = -> Origin020
  Tip = -> Pad016
COMPONENT P16 — geometry summary ("KeyColumnCutNC4"; no construction recipe available for this part):
  bounding box: 127.3 x 45.9 x 19.3 mm
  tessellated surface: 584 triangles
  volume: 6885 mm^3 (6% of its bounding box)
COMPONENT P17 — geometry summary ("ThumbCluster"; no construction recipe available for this part):
  bounding box: 75.2 x 66.0 x 40.8 mm
  tessellated surface: 904 triangles
  volume: 16076 mm^3 (8% of its bounding box)
COMPONENT P18 — recipe-attached ("KeycapThumb", modeled in this document).
Construction recipe (the document's own serialized feature program — sketch geometry with constraints, then the solid features built on it; lengths are millimeters unless a unit is written):

FEATURE [Sketcher::SketchObject] Sketch009
  FullyConstrained = false
  MapMode = 5
  Placement = pos=(0,0,0) rot=(0.57735,0.57735,0.57735;2.0944rad)
  Support = -> [YZ_Plane008]
  sketch-geometry (9):
    g0: LineSegment StartX=39.5 StartY=9 StartZ=0 EndX=22.8616 EndY=9 EndZ=0
    g1: LineSegment StartX=22.8616 StartY=9 StartZ=0 EndX=22.8616 EndY=3 EndZ=0
    g2: LineSegment StartX=22.8616 StartY=3 StartZ=0 EndX=20.2616 EndY=3 EndZ=0
    g3: LineSegment StartX=20.2616 StartY=3 StartZ=0 EndX=18.2616 EndY=5 EndZ=0
    g4: LineSegment StartX=18.2616 StartY=5 StartZ=0 EndX=18.2616 EndY=10.5 EndZ=0
    g5: LineSegment StartX=39.5 StartY=11.5 StartZ=0 EndX=39.5 EndY=9 EndZ=0
    g6: LineSegment StartX=18.2616 StartY=10.5 StartZ=0 EndX=32.4662 EndY=16.0518 EndZ=0
    g7: LineSegment StartX=32.4662 StartY=16.0518 StartZ=0 EndX=39.5 EndY=13.7315 EndZ=0
    g8: LineSegment StartX=39.5 StartY=11.5 StartZ=0 EndX=39.5 EndY=13.7315 EndZ=0
  constraints (22):
    c: Horizontal(g0)
    c: Coincident(g0,g1)
    c: Vertical(g1)
    c: Coincident(g1,g2)
    c: Coincident(g2,g3)
    c: Coincident(g3,g4)
    c: Vertical(g4)
    c: Coincident(g5,g0)
    c: Vertical(g5)
    c: DistanceX(g0) = 39.5
    c: DistanceY(g0) = 9
    c: DistanceY(g5,g5) = 2.5
    c: Horizontal(g2)
    c: DistanceX(g2,g2) = 2.6
    c: Angle(g2,g3) = 2.35619
    c: DistanceY(g1,g1) = 6
    c: DistanceY(g2,g3) = 2
    c: Coincident(g6,g7)
    c: Coincident(g8,g5)
    c: Coincident(g8,g7)
    c: Vertical(g8)
    c: Coincident(g6,g4)
FEATURE [PartDesign::Pad] Pad006
  Direction = (1,-2e-16,3e-16)
  Length = 6.5
  Length2 = 10
  Midplane = true
  Placement = pos=(0,0,0) rot=(1,1,1;2.0944rad)
  Profile = -> Sketch009
  ReferenceAxis = -> Sketch009 [N_Axis]
  Type = 0
FEATURE [PartDesign::Body] Body008  label="TRRS-Holder"
  Group = -> [Sketch009,Pad006]
  Origin = -> Origin008
  Placement = pos=(10.5,0,0) rot=(0,0,1;0rad)
  Tip = -> Pad006
COMPONENT P19 — recipe-attached ("KeyColumnBlankN", a linked part whose construction recipe lives in a companion FreeCAD document of the same project; that document's serialized recipe follows).
Construction recipe (the companion document, serialized — sketch geometry with constraints, then the solid features built on it; lengths are millimeters unless a unit is written):

FCSTD DOCUMENT  (FreeCAD 0.21R33668 +26 (Git))
Label: KeyColumn2
License: All rights reserved
LicenseURL: http://en.wikipedia.org/wiki/All_rights_reserved
objects: App::Link×6, Sketcher::SketchObject×4, PartDesign::Body×4, Part::Compound×4, Part::Refine×3, PartDesign::SubShapeBinder×3, Part::Offset2D×2, Part::Extrusion×2, PartDesign::Pad×2, Part::Cut×2, App::DocumentObjectGroup×2, Spreadsheet::Sheet×1
note: 28 computed .brp shape members not serialized (recipe doc carries the construction recipe); baked Part::Feature solids carry a one-line shape summary decoded from their .brp
EXTERNAL_REF file=../components/MX_Switches.FCStd obj=Body008
EXTERNAL_REF file=../components/MX-Latch-Subtractor2.FCStd obj=Body001

FEATURE [Spreadsheet::Sheet] Spreadsheet  label="S"
  cells = B1=172.75; B2==180 - B1; B3=21; A4='Well Angle; B4(WellAngle)=159; C4='deg; D4=159; A5='Knucle Spacing; B5(KnuckleSpace)==7.25 mm; A6='End Slope; B6(EndSlope)=22.5; C6='deg; D6='Bottom palm; A7='End Slope B; B7(EndSlopeB)=22.5; C7='deg; D7='Top tips
FEATURE [Sketcher::SketchObject] Sketch
  FullyConstrained = true
  MapMode = 5
  Placement = pos=(0,0,0) rot=(0.57735,0.57735,0.57735;2.0944rad)
  Support = -> [YZ_Plane]
  expr: Constraints[14] = <<S>>.KnuckleSpace
  expr: Constraints[18] = <<S>>.WellAngle
  expr: Constraints[19] = <<S>>.WellAngle
  expr: Constraints[20] = <<S>>.EndSlopeB
  expr: Constraints[21] = <<S>>.EndSlope
  sketch-geometry (9):
    g0: LineSegment StartX=-29.8362 StartY=7.29053 StartZ=0 EndX=-12.0982 EndY=0.481542 EndZ=0
    g1: LineSegment StartX=-9.5 StartY=0 StartZ=0 EndX=9.5 EndY=0 EndZ=0
    g2: LineSegment StartX=12.0982 StartY=0.481542 StartZ=0 EndX=29.8362 EndY=7.29053 EndZ=0
    g3: ArcOfCircle CenterX=-32.4344 CenterY=0.522075 CenterZ=0 NormalX=0 NormalY=0 NormalZ=1 AngleXU=0 Radius=7.25 StartAngle=1.20428 EndAngle=1.9635
    g4: LineSegment StartX=-35.2088 StartY=7.2202 StartZ=0 EndX=-72.164 EndY=-8.08714 EndZ=0
    g5: ArcOfCircle CenterX=32.4344 CenterY=0.522075 CenterZ=0 NormalX=0 NormalY=0 NormalZ=1 AngleXU=0 Radius=7.25 StartAngle=1.1781 EndAngle=1.93732
    g6: LineSegment StartX=35.2088 StartY=7.2202 StartZ=0 EndX=52.6399 EndY=0 EndZ=0
    g7: ArcOfCircle CenterX=-9.5 CenterY=7.25 CenterZ=0 NormalX=0 NormalY=0 NormalZ=1 AngleXU=0 Radius=7.25 StartAngle=4.34587 EndAngle=4.71239
    g8: ArcOfCircle CenterX=9.5 CenterY=7.25 CenterZ=0 NormalX=0 NormalY=0 NormalZ=1 AngleXU=0 Radius=7.25 StartAngle=4.71239 EndAngle=5.07891
  constraints (23):
    c: Horizontal(g1)
    c: Symmetric(g1,g1,g-1)
    c: Equal(g1,g2)
    c: Equal(g1,g0)
    c: Tangent(g4,g3) = -1.5708
    c: Tangent(g6,g5) = 1.5708
    c: PointOnObject(g6,g-1)
    c: Tangent(g0,g3) = 1.5708
    c: Tangent(g5,g2) = 1.5708
    c: Tangent(g8,g2) = -1.5708
    c: Tangent(g8,g1) = -1.5708
    c: Tangent(g7,g1) = -1.5708
    c: Tangent(g7,g0) = -1.5708
    c: Distance(g1) = 19
    c: Radius(g3) = 7.25
    c: Equal(g3,g7)
    c: Equal(g7,g8)
    c: Equal(g8,g5)
    c: Angle(g1,g0) = 2.77507
    c: Angle(g2,g1) = 2.77507
    c: Angle(g6,g-1) = 0.392699
    c: Angle(g-1,g4) = 0.392699
    c: Distance(g4) = 40
FEATURE [PartDesign::Body] Body  label="SketchProfile"
  Group = -> [Sketch]
  Origin = -> Origin
FEATURE [Part::Offset2D] Offset2D
  Fill = false
  Intersection = false
  Join = 2
  Mode = 1
  SelfIntersection = false
  Source = -> Sketch
  Value = 1.8
FEATURE [Part::Extrusion] Extrude001  label="KeyColumnBase"
  Base = -> Offset2D
  Dir = (1,0,0)
  DirMode = 0
  FaceMakerClass = Part::FaceMakerBullseye
  LengthFwd = 19
  LengthRev = 0
  Solid = true
  Symmetric = true
FEATURE [App::Link] Link  label="MXSwitch100Nice"
  AttacherType = Attacher::AttachEngine3D
  LinkPlacement = pos=(3.6e-15,20.3221,5.56648) rot=(1,0,0;0.366519rad)
  LinkedObject = -> <external ../components/MX_Switches.FCStd>#Body008
  MapMode = 2
  Placement = pos=(3.6e-15,20.3221,5.56648) rot=(1,0,0;0.366519rad)
FEATURE [App::Link] Link001  label="MXSwitch100Nice001"
  AttacherType = Attacher::AttachEngine3D
  LinkPlacement = pos=(0,-1.8e-15,1.8) rot=(0,0,1;0rad)
  LinkedObject = -> Link
  MapMode = 2
  Placement = pos=(0,-1.8e-15,1.8) rot=(0,0,1;0rad)
FEATURE [App::Link] Link002  label="MXSwitch100Nice002"
  AttacherType = Attacher::AttachEngine3D
  LinkPlacement = pos=(-8.9e-15,-20.3221,5.56648) rot=(-1,0,0;0.366519rad)
  LinkedObject = -> Link001
  MapMode = 2
  Placement = pos=(-8.9e-15,-20.3221,5.56648) rot=(-1,0,0;0.366519rad)
FEATURE [App::Link] Link003  label="MX-Latch-Subtractor2N"
  AttacherType = Attacher::AttachEngine3D
  LinkPlacement = pos=(3.6e-15,20.3221,5.56648) rot=(1,0,0;0.366519rad)
  LinkedObject = -> <external ../components/MX-Latch-Subtractor2.FCStd>#Body001
  MapMode = 2
  Placement = pos=(3.6e-15,20.3221,5.56648) rot=(1,0,0;0.366519rad)
FEATURE [App::Link] Link004  label="MX-Latch-Subtractor2N001"
  AttacherType = Attacher::AttachEngine3D
  LinkPlacement = pos=(0,-1.8e-15,1.8) rot=(0,0,1;0rad)
  LinkedObject = -> Link003
  MapMode = 2
  Placement = pos=(0,-1.8e-15,1.8) rot=(0,0,1;0rad)
FEATURE [App::Link] Link005  label="MX-Latch-Subtractor2N002"
  AttacherType = Attacher::AttachEngine3D
  LinkPlacement = pos=(-8.9e-15,-20.3221,5.56648) rot=(-1,0,0;0.366519rad)
  LinkedObject = -> Link004
  MapMode = 2
  Placement = pos=(-8.9e-15,-20.3221,5.56648) rot=(-1,0,0;0.366519rad)
FEATURE [Part::Compound] Compound  label="MXSwitchC"
  Links = -> [Link,Link001,Link002]
FEATURE [Part::Compound] Compound001  label="SubtractorC"
  Links = -> [Link005,Link003,Link004]
FEATURE [Sketcher::SketchObject] Sketch001
  FullyConstrained = false
  MapMode = 5
  Placement = pos=(0,0,0) rot=(0.57735,0.57735,0.57735;2.0944rad)
  Support = -> [YZ_Plane002]
  expr: Constraints[17] = <<S>>.KnuckleSpace
  expr: Constraints[5] = <<S>>.KnuckleSpace
  sketch-geometry (7):
    g0: LineSegment StartX=-31.0713 StartY=7.8 StartZ=0 EndX=8.10798 EndY=0.13489 EndZ=0
    g1: LineSegment StartX=12.0982 StartY=0.481542 StartZ=0 EndX=29.8362 EndY=7.29053 EndZ=0
    g2: ArcOfCircle CenterX=-32.4633 CenterY=0.68489 CenterZ=0 NormalX=0 NormalY=0 NormalZ=1 AngleXU=0 Radius=7.25 StartAngle=1.37759 EndAngle=1.78024
    g3: LineSegment StartX=-33.9706 StartY=7.77646 StartZ=0 EndX=-53.5336 EndY=3.61823 EndZ=0
    g4: ArcOfCircle CenterX=32.4344 CenterY=0.522075 CenterZ=0 NormalX=0 NormalY=0 NormalZ=1 AngleXU=0 Radius=7.25 StartAngle=0.610865 EndAngle=1.93732
    g5: LineSegment StartX=38.3732 StartY=4.6805 StartZ=0 EndX=49.8447 EndY=-11.7025 EndZ=0
    g6: ArcOfCircle CenterX=9.5 CenterY=7.25 CenterZ=0 NormalX=0 NormalY=0 NormalZ=1 AngleXU=0 Radius=7.25 StartAngle=4.51919 EndAngle=5.07891
  constraints (18):
    c: Tangent(g3,g2) = -1.5708
    c: Tangent(g5,g4) = 1.5708
    c: Tangent(g0,g2) = 1.5708
    c: Tangent(g4,g1) = 1.5708
    c: Tangent(g6,g1) = -1.5708
    c: Radius(g2) = 7.25
    c: Equal(g6,g4)
    c: Angle(g5,g-1) = 0.959931
    c: Angle(g-1,g3) = 0.20944
    c: Distance(g1) = 19
    c: DistanceX(g1) = 12.0982
    c: DistanceY(g1) = 0.481542
    c: DistanceX(g1) = 29.8362
    c: Tangent(g6,g0) = -1.5708
    c: DistanceY(g-1,g0) = 7.8
    c: Distance(g3) = 20
    c: Distance(g5) = 20
    c: Radius(g4) = 7.25
FEATURE [PartDesign::Body] Body002  label="SketchProfileAlt"
  Group = -> [Sketch001]
  Origin = -> Origin002
FEATURE [Part::Offset2D] Offset2D001
  Fill = false
  Intersection = false
  Join = 0
  Mode = 1
  SelfIntersection = false
  Source = -> Sketch001
  Value = 1.8
FEATURE [Part::Extrusion] Extrude  label="KeyColumnBlank"
  Base = -> Offset2D001
  Dir = (1,-2e-16,2e-16)
  DirMode = 2
  FaceMakerClass = Part::FaceMakerBullseye
  LengthFwd = 19
  LengthRev = 0
  Solid = true
  Symmetric = true
FEATURE [Part::Refine] Extrude003  label="KeyColumnBlankN"
  Source = -> Extrude
FEATURE [PartDesign::SubShapeBinder] Binder
  BindCopyOnChange = 0
  BindMode = 0
  ClaimChildren = false
  Context = -> Body003 [Binder.]
  Fuse = false
  MakeFace = true
  OffsetFill = false
  OffsetIntersection = false
  OffsetJoinType = 0
  OffsetOpenResult = false
  PartialLoad = false
  Relative = true
  Support = -> [Extrude001[Face21]]
  _Version = 2
FEATURE [Sketcher::SketchObject] Sketch002
  ExternalGeometry = -> [Binder]
  FullyConstrained = true
  MapMode = 5
  Placement = pos=(0,0,0) rot=(0.57735,0.57735,0.57735;2.0944rad)
  Support = -> [YZ_Plane003]
  sketch-geometry (4):
    g0: LineSegment StartX=53.3288 StartY=1.66298 StartZ=0 EndX=56.6547 EndY=0.285323 EndZ=0
    g1: LineSegment StartX=56.6547 StartY=0.285323 StartZ=0 EndX=55.2771 EndY=-3.04064 EndZ=0
    g2: LineSegment StartX=55.2771 StartY=-3.04064 StartZ=0 EndX=51.9511 EndY=-1.66298 EndZ=0
    g3: LineSegment StartX=51.9511 StartY=-1.66298 StartZ=0 EndX=53.3288 EndY=1.66298 EndZ=0
  constraints (10):
    c: Coincident(g0,g-3)
    c: Coincident(g0,g1)
    c: Coincident(g1,g2)
    c: Coincident(g2,g-4)
    c: Coincident(g2,g3)
    c: Coincident(g3,g0)
    c: Perpendicular(g0,g3)
    c: Perpendicular(g2,g3)
    c: Perpendicular(g1,g2)
    c: Equal(g3,g0)
FEATURE [PartDesign::Pad] Pad
  Direction = (1,-2e-16,3e-16)
  Length = 20
  Length2 = 10
  Midplane = true
  Placement = pos=(0,0,0) rot=(0.57735,0.57735,0.57735;2.0944rad)
  Profile = -> Sketch002
  ReferenceAxis = -> Sketch002 [N_Axis]
  Type = 0
FEATURE [PartDesign::Body] Body003  label="TrimA"
  Group = -> [Binder,Sketch002,Pad]
  Origin = -> Origin003
  Tip = -> Pad
FEATURE [PartDesign::SubShapeBinder] Binder001
  BindCopyOnChange = 0
  BindMode = 0
  ClaimChildren = false
  Context = -> Body004 [Binder001.]
  Fuse = false
  MakeFace = true
  OffsetFill = false
  OffsetIntersection = false
  OffsetJoinType = 0
  OffsetOpenResult = false
  PartialLoad = false
  Relative = true
  _Version = 2
FEATURE [Sketcher::SketchObject] Sketch003
  ExternalGeometry = -> [Binder001]
  FullyConstrained = true
  MapMode = 5
  Placement = pos=(0,0,0) rot=(0.57735,0.57735,0.57735;2.0944rad)
  Support = -> [YZ_Plane004]
  sketch-geometry (4):
    g0: LineSegment StartX=-72.8528 StartY=-6.42415 StartZ=0 EndX=-71.4752 EndY=-9.75012 EndZ=0
    g1: LineSegment StartX=-71.4752 StartY=-9.75012 StartZ=0 EndX=-74.8011 EndY=-11.1278 EndZ=0
    g2: LineSegment StartX=-74.8011 StartY=-11.1278 StartZ=0 EndX=-76.1788 EndY=-7.80181 EndZ=0
    g3: LineSegment StartX=-76.1788 StartY=-7.80181 StartZ=0 EndX=-72.8528 EndY=-6.42415 EndZ=0
  constraints (10):
    c: Coincident(g0,g-3)
    c: Coincident(g0,g-4)
    c: Coincident(g0,g1)
    c: Coincident(g1,g2)
    c: Coincident(g2,g3)
    c: Coincident(g3,g0)
    c: Perpendicular(g0,g3)
    c: Perpendicular(g0,g1)
    c: Perpendicular(g1,g2)
    c: Equal(g0,g1)
FEATURE [PartDesign::Pad] Pad001
  Direction = (1,-2e-16,3e-16)
  Length = 20
  Length2 = 10
  Midplane = true
  Placement = pos=(0,0,0) rot=(0.57735,0.57735,0.57735;2.0944rad)
  Profile = -> Sketch003
  ReferenceAxis = -> Sketch003 [N_Axis]
  Type = 0
FEATURE [PartDesign::SubShapeBinder] Binder002
  BindCopyOnChange = 0
  BindMode = 0
  ClaimChildren = false
  Context = -> Body004 [Binder002.]
  Fuse = false
  MakeFace = true
  OffsetFill = false
  OffsetIntersection = false
  OffsetJoinType = 0
  OffsetOpenResult = false
  PartialLoad = false
  Relative = true
  Support = -> [Extrude001[Face21]]
  _Version = 2
FEATURE [PartDesign::Body] Body004  label="TrimB"
  Group = -> [Binder001,Sketch003,Pad001,Binder002]
  Origin = -> Origin004
  Tip = -> Pad001
FEATURE [Part::Compound] Compound002  label="EndTrimmers"
  Links = -> [Body003,Body004]
FEATURE [Part::Cut] Cut002  label="KeyColumnTrim"
  Base = -> Extrude001
  Tool = -> Compound002
FEATURE [Part::Cut] Cut004  label="KeyColumnCut"
  Base = -> Cut002
  Tool = -> Compound001
FEATURE [Part::Refine] Cut001  label="KeyColumnCutN"
  Source = -> Cut004
FEATURE [Part::Compound] Compound003  label="KeyColumnCaps"
  Links = -> [Cut002,Compound]
FEATURE [App::DocumentObjectGroup] Group001  label="Working"
  Group = -> [Cut004,Body,Compound,Body002,Extrude,Compound003]
FEATURE [Part::Refine] Compound004  label="KeyColumnCapsN"
  Source = -> Compound003
FEATURE [App::DocumentObjectGroup] Group  label="Refined Copies"
  Group = -> [Extrude003,Cut001,Compound004]
COMPONENT P20 — recipe-attached ("TRRS-PJ-313B", a linked part whose construction recipe lives in a companion FreeCAD document of the same project; that document's serialized recipe follows).
Construction recipe (the companion document, serialized — sketch geometry with constraints, then the solid features built on it; lengths are millimeters unless a unit is written):

FCSTD DOCUMENT  (FreeCAD 0.21R33668 +26 (Git))
Label: PJ-313B__JACK35F-4P-PCB
License: All rights reserved
LicenseURL: http://en.wikipedia.org/wiki/All_rights_reserved
objects: Sketcher::SketchObject×5, PartDesign::Pad×3, PartDesign::Body×2, Part::Refine×2, App::DocumentObjectGroup×2, PartDesign::Mirrored×1, PartDesign::LinearPattern×1, PartDesign::MultiTransform×1, PartDesign::AdditiveLoft×1
note: 20 computed .brp shape members not serialized (recipe doc carries the construction recipe); baked Part::Feature solids carry a one-line shape summary decoded from their .brp

FEATURE [Sketcher::SketchObject] Sketch
  FullyConstrained = true
  MapMode = 5
  Placement = pos=(0,0,0) rot=(0.57735,0.57735,0.57735;2.0944rad)
  Support = -> [YZ_Plane]
  sketch-geometry (4):
    g0: LineSegment StartX=-14.6 StartY=5 StartZ=0 EndX=0 EndY=5 EndZ=0
    g1: LineSegment StartX=0 StartY=5 StartZ=0 EndX=0 EndY=0 EndZ=0
    g2: LineSegment StartX=0 StartY=0 StartZ=0 EndX=-14.6 EndY=0 EndZ=0
    g3: LineSegment StartX=-14.6 StartY=0 StartZ=0 EndX=-14.6 EndY=5 EndZ=0
  constraints (11):
    c: Coincident(g0,g1)
    c: Coincident(g1,g2)
    c: Coincident(g2,g3)
    c: Coincident(g3,g0)
    c: Horizontal(g0)
    c: Horizontal(g2)
    c: Vertical(g1)
    c: Vertical(g3)
    c: Coincident(g1,g-1)
    c: DistanceX(g0,g0) = 14.6
    c: DistanceY(g3,g3) = 5
FEATURE [PartDesign::Pad] Pad
  Direction = (1,-2e-16,3e-16)
  Length = 5
  Length2 = 10
  Midplane = true
  Placement = pos=(0,0,0) rot=(0.57735,0.57735,0.57735;2.0944rad)
  Profile = -> Sketch
  ReferenceAxis = -> Sketch [N_Axis]
  Type = 0
FEATURE [Sketcher::SketchObject] Sketch001
  ExternalGeometry = -> [Pad]
  FullyConstrained = true
  MapMode = 5
  Placement = pos=(0,0,0) rot=(0.57735,0.57735,0.57735;4.18879rad)
  Support = -> [Pad]
  sketch-geometry (2):
    g0: Circle CenterX=2.5 CenterY=-1e-15 CenterZ=0 NormalX=0 NormalY=0 NormalZ=1 AngleXU=0 Radius=1.8
    g1: Circle CenterX=2.5 CenterY=-1e-15 CenterZ=0 NormalX=0 NormalY=0 NormalZ=1 AngleXU=0 Radius=2.5
  constraints (4):
    c: Radius(g0) = 1.8
    c: Symmetric(g-4,g-3,g0)
    c: Coincident(g1,g0)
    c: Radius(g1) = 2.5
FEATURE [PartDesign::Pad] Pad001
  BaseFeature = -> Pad
  Direction = (4e-16,1,-2e-16)
  Length = 2.5
  Length2 = 10
  Placement = pos=(0,0,0) rot=(0.57735,0.57735,0.57735;2.0944rad)
  Profile = -> Sketch001
  ReferenceAxis = -> Sketch001 [N_Axis]
  Type = 0
FEATURE [Sketcher::SketchObject] Sketch002
  AttachmentOffset = pos=(0,0,2.5) rot=(0,0,1;0rad)
  FullyConstrained = true
  MapMode = 5
  Placement = pos=(0,0,2.5) rot=(0,0,1;0rad)
  Support = -> [XY_Plane]
  expr: Constraints[12] = 1.8 mm + 3.2 mm * 3
  sketch-geometry (5):
    g0: LineSegment StartX=-3.25 StartY=-10.75 StartZ=0 EndX=-2.45 EndY=-10.75 EndZ=0
    g1: LineSegment StartX=-2.45 StartY=-10.75 StartZ=0 EndX=-2.45 EndY=-12.05 EndZ=0
    g2: LineSegment StartX=-2.45 StartY=-12.05 StartZ=0 EndX=-3.25 EndY=-12.05 EndZ=0
    g3: LineSegment StartX=-3.25 StartY=-12.05 StartZ=0 EndX=-3.25 EndY=-10.75 EndZ=0
    g4: GeomPoint X=-2.85 Y=-11.4 Z=0
  constraints (13):
    c: Coincident(g0,g1)
    c: Coincident(g1,g2)
    c: Coincident(g2,g3)
    c: Coincident(g3,g0)
    c: Horizontal(g0)
    c: Horizontal(g2)
    c: Vertical(g1)
    c: Vertical(g3)
    c: DistanceY(g3,g3) = 1.3
    c: DistanceX(g0,g0) = 0.8
    c: Symmetric(g0,g1,g4)
    c: DistanceX(g4,g-1) = 2.85
    c: DistanceY(g4,g-1) = 11.4
FEATURE [PartDesign::Pad] Pad002
  BaseFeature = -> Pad001
  Direction = (0,0,1)
  Length = 5.5
  Length2 = 10
  Placement = pos=(0,0,0) rot=(0.57735,0.57735,0.57735;2.0944rad)
  Profile = -> Sketch002
  ReferenceAxis = -> Sketch002 [N_Axis]
  Reversed = true
  Type = 0
FEATURE [PartDesign::Mirrored] Mirrored
  MirrorPlane = -> Sketch002 [V_Axis]
  Placement = pos=(0,0,0) rot=(1,1,1;2.0944rad)
FEATURE [PartDesign::LinearPattern] LinearPattern
  Direction = -> Y_Axis
  Length = 9.6
  Occurrences = 4
  Placement = pos=(0,0,0) rot=(1,1,1;2.0944rad)
FEATURE [PartDesign::MultiTransform] MultiTransform
  BaseFeature = -> Pad002
  Originals = -> [Pad002]
  Placement = pos=(0,0,0) rot=(0.57735,0.57735,0.57735;2.0944rad)
  Transformations = -> [Mirrored,LinearPattern]
FEATURE [PartDesign::Body] Body  label="TRRS-PJ-313B"
  Group = -> [Sketch,Pad,Sketch001,Pad001,Sketch002,Pad002,MultiTransform,Mirrored,LinearPattern]
  Origin = -> Origin
  Tip = -> MultiTransform
FEATURE [Part::Refine] MultiTransform001  label="TRRS-PJ-313BN"
  Source = -> MultiTransform
FEATURE [Sketcher::SketchObject] Sketch003
  FullyConstrained = true
  MapMode = 5
  Placement = pos=(0,0,0) rot=(1,0,0;1.5708rad)
  Support = -> [XZ_Plane001]
  sketch-geometry (1):
    g0: Circle CenterX=0 CenterY=2.5 CenterZ=0 NormalX=0 NormalY=0 NormalZ=1 AngleXU=0 Radius=2.5
  constraints (3):
    c: Diameter(g0) = 5
    c: DistanceY(g-1,g0) = 2.5
    c: Vertical(g0,g-1)
FEATURE [Sketcher::SketchObject] Sketch004
  AttachmentOffset = pos=(0,0,-3) rot=(0,0,1;0rad)
  FullyConstrained = true
  MapMode = 5
  Placement = pos=(0,3,7e-16) rot=(1,0,0;1.5708rad)
  Support = -> [XZ_Plane001]
  sketch-geometry (1):
    g0: Circle CenterX=0 CenterY=2.5 CenterZ=0 NormalX=0 NormalY=0 NormalZ=1 AngleXU=0 Radius=3
  constraints (3):
    c: Diameter(g0) = 6
    c: DistanceY(g-1,g0) = 2.5
    c: Vertical(g0,g-1)
FEATURE [PartDesign::AdditiveLoft] AdditiveLoft
  Closed = false
  Placement = pos=(0,0,0) rot=(1,0,0;1.5708rad)
  Profile = -> Sketch003
  Ruled = false
  Sections = -> [Sketch004]
FEATURE [PartDesign::Body] Body001  label="TRRS-Cutter"
  Group = -> [Sketch003,Sketch004,AdditiveLoft]
  Origin = -> Origin001
  Placement = pos=(0,6.5,0) rot=(0,0,1;0rad)
  Tip = -> AdditiveLoft
FEATURE [Part::Refine] Body002  label="TRRS-CutterN"
  Source = -> Body001
FEATURE [App::DocumentObjectGroup] Group  label="Parts"
  Group = -> [Body,Body001]
FEATURE [App::DocumentObjectGroup] Group001  label="Refined Copies"
  Group = -> [Body002,MultiTransform001]
COMPONENT P21 — recipe-attached ("MCU-Cutter", modeled in this document).
Construction recipe (the document's own serialized feature program — sketch geometry with constraints, then the solid features built on it; lengths are millimeters unless a unit is written):

FEATURE [Sketcher::SketchObject] Sketch004
  FullyConstrained = false
  MapMode = 5
  Support = -> [XY_Plane005]
  sketch-geometry (6):
    g0: LineSegment StartX=-16.8908 StartY=-67.2591 StartZ=0 EndX=1.39342 EndY=-63.2974 EndZ=0
    g1: LineSegment StartX=1.39342 StartY=-63.2974 StartZ=0 EndX=21.8742 EndY=-61.6751 EndZ=0
    g2: LineSegment StartX=21.8742 StartY=-61.6751 StartZ=0 EndX=92.4415 EndY=-51.3334 EndZ=0
    g3: LineSegment StartX=92.4415 StartY=-51.3334 StartZ=0 EndX=92.4415 EndY=-99.9441 EndZ=0
    g4: LineSegment StartX=92.4415 StartY=-99.9441 StartZ=0 EndX=-16.8908 EndY=-99.9441 EndZ=0
    g5: LineSegment StartX=-16.8908 StartY=-99.9441 StartZ=0 EndX=-16.8908 EndY=-67.2591 EndZ=0
  constraints (9):
    c: Coincident(g0,g1)
    c: Coincident(g1,g2)
    c: Coincident(g2,g3)
    c: Vertical(g3)
    c: Coincident(g3,g4)
    c: Horizontal(g4)
    c: Coincident(g4,g5)
    c: Coincident(g5,g0)
    c: Vertical(g5)
FEATURE [PartDesign::Pad] Pad004
  Direction = (0,0,1)
  Length = 60
  Length2 = 10
  Midplane = true
  Profile = -> Sketch004
  ReferenceAxis = -> Sketch004 [N_Axis]
  Type = 0
FEATURE [PartDesign::Body] Body005  label="ColumnCutterBottom"
  Group = -> [Sketch004,Pad004]
  Origin = -> Origin005
  Tip = -> Pad004
COMPONENT P22 — recipe-attached ("TRRS-Cutter", modeled in this document).
Construction recipe (the document's own serialized feature program — sketch geometry with constraints, then the solid features built on it; lengths are millimeters unless a unit is written):

FEATURE [Sketcher::SketchObject] Sketch001
  FullyConstrained = false
  MapMode = 5
  Support = -> [XY_Plane002]
  sketch-geometry (7):
    g0: LineSegment StartX=-31.9823 StartY=64.42 StartZ=0 EndX=-31.9823 EndY=38.6825 EndZ=0
    g1: LineSegment StartX=-31.9823 StartY=38.6825 StartZ=0 EndX=51.7413 EndY=38.6825 EndZ=0
    g2: LineSegment StartX=51.7413 StartY=38.6825 StartZ=0 EndX=84.9247 EndY=25.1531 EndZ=0
    g3: LineSegment StartX=84.9247 StartY=25.1531 StartZ=0 EndX=98.4266 EndY=4.34688 EndZ=0
    g4: LineSegment StartX=98.4266 StartY=4.34688 StartZ=0 EndX=116.798 EndY=4.34688 EndZ=0
    g5: LineSegment StartX=116.798 StartY=4.34688 StartZ=0 EndX=116.798 EndY=64.42 EndZ=0
    g6: LineSegment StartX=116.798 StartY=64.42 StartZ=0 EndX=-31.9823 EndY=64.42 EndZ=0
  constraints (12):
    c: Vertical(g0)
    c: Coincident(g0,g1)
    c: Horizontal(g1)
    c: Coincident(g1,g2)
    c: Coincident(g2,g3)
    c: Coincident(g3,g4)
    c: Horizontal(g4)
    c: Coincident(g4,g5)
    c: Vertical(g5)
    c: Coincident(g5,g6)
    c: Coincident(g6,g0)
    c: Horizontal(g6)
FEATURE [PartDesign::Pad] Pad001
  Direction = (0,0,1)
  Length = 20
  Length2 = 10
  Profile = -> Sketch001
  ReferenceAxis = -> Sketch001 [N_Axis]
  Type = 0
FEATURE [PartDesign::Body] Body002  label="ColumnCutterTop"
  Group = -> [Sketch001,Pad001]
  Origin = -> Origin002
  Tip = -> Pad001
COMPONENT P23 — geometry summary ("HeatsetTopLeftA"; no construction recipe available for this part):
  bounding box: 13.9 x 10.5 x 7.0 mm
  tessellated surface: 1,716 triangles
  volume: 666 mm^3 (65% of its bounding box)
  symmetry: mirror-symmetric across its x mid-plane
COMPONENT P24 — geometry summary ("HeatsetBotRightA"; no construction recipe available for this part):
  bounding box: 13.8 x 11.4 x 7.0 mm
  tessellated surface: 1,716 triangles
  volume: 666 mm^3 (61% of its bounding box)
COMPONENT P25 — geometry summary ("KeycapFinger001"; no construction recipe available for this part):
  bounding box: 27.3 x 21.7 x 21.3 mm
  tessellated surface: 580 triangles
  volume: 4560 mm^3 (36% of its bounding box)
COMPONENT P26 — geometry summary ("HeatsetBotLeftA"; no construction recipe available for this part):
  bounding box: 9.0 x 9.0 x 7.0 mm
  tessellated surface: 2,012 triangles
  volume: 393 mm^3 (69% of its bounding box)
  symmetry: 6-fold rotationally symmetric about the z axis; mirror-symmetric across its x mid-plane
COMPONENT P27 — geometry summary ("PlateWithHolesN"; no construction recipe available for this part):
  bounding box: 140.9 x 109.3 x 2.0 mm
  tessellated surface: 4,632 triangles
  volume: 24142 mm^3 (78% of its bounding box)
  symmetry: mirror-symmetric across its z mid-plane
PROVENANCE & LICENSES
A FreeCAD (.FCStd) document from a public repository crawl; recipes are the document's own serialized feature recipes (and, for linked parts, companion documents' recipes).
License: mit.
